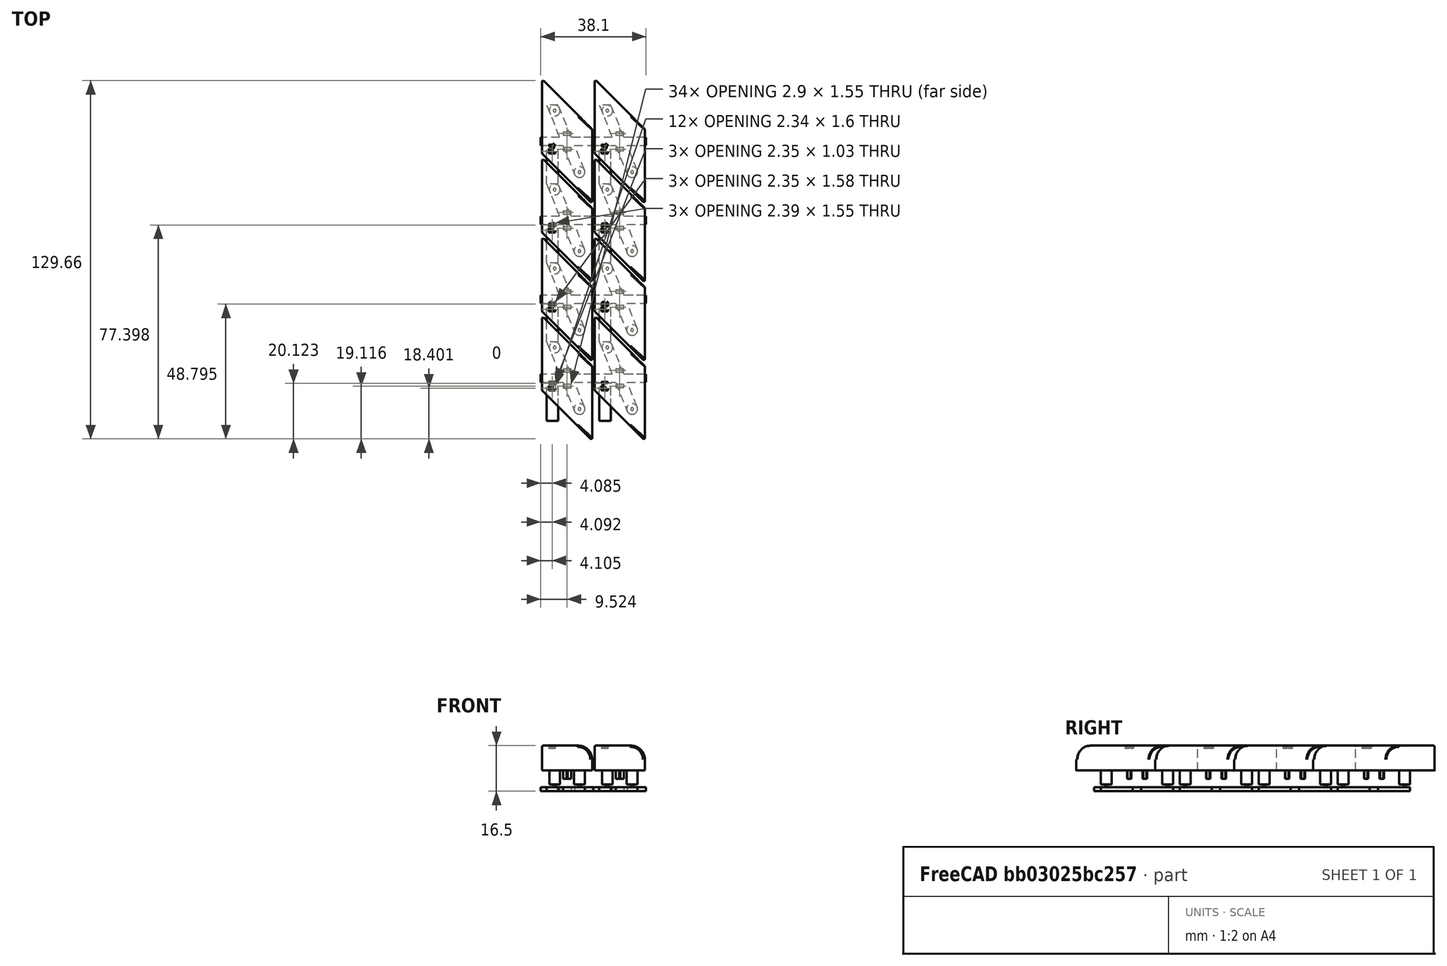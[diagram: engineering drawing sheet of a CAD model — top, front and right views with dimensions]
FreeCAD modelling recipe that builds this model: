
FCSTD DOCUMENT  (FreeCAD 0.21R33771 (Git))
Label: ConsoleXE-F1-4
License: All rights reserved
LicenseURL: http://en.wikipedia.org/wiki/All_rights_reserved
objects: Sketcher::SketchObject×6, PartDesign::Pad×5, Part::Extrusion×5, Part::FeaturePython×4, Part::Compound×4, Part::Part2DObjectPython×4, PartDesign::Body×2, PartDesign::Pocket×1, PartDesign::Line×1, PartDesign::Point×1, PartDesign::Fillet×1, PartDesign::FeatureBase×1, Part::Cut×1, Mesh::Feature×1
note: 43 computed .brp shape members not serialized (recipe doc carries the construction recipe); baked Part::Feature solids carry a one-line shape summary decoded from their .brp

FEATURE [Sketcher::SketchObject] Sketch  label="SideSketch"
  FullyConstrained = true
  MapMode = 5
  Placement = pos=(0,0,0) rot=(1,0,0;1.5708rad)
  Support = -> [XZ_Plane]
  expr: Constraints[10] = 26.4 * cos(45) - 0.5
  sketch-geometry (5):
    g0: LineSegment StartX=0 StartY=0 StartZ=0 EndX=0 EndY=9 EndZ=0
    g1: LineSegment StartX=0 StartY=9 StartZ=0 EndX=13.1676 EndY=9 EndZ=0
    g2: ArcOfCircle CenterX=13.1676 CenterY=4 CenterZ=0 NormalX=0 NormalY=0 NormalZ=1 AngleXU=0 Radius=5 StartAngle=0 EndAngle=1.5708
    g3: LineSegment StartX=18.1676 StartY=4 StartZ=0 EndX=18.1676 EndY=0 EndZ=0
    g4: LineSegment StartX=18.1676 StartY=0 StartZ=0 EndX=0 EndY=0 EndZ=0
  constraints (14):
    c: Coincident(g-1,g0)
    c: PointOnObject(g0,g-2)
    c: Coincident(g0,g1)
    c: Horizontal(g1)
    c: Tangent(g1,g2) = 1.5708
    c: Coincident(g2,g3)
    c: PointOnObject(g3,g-1)
    c: Vertical(g3)
    c: Coincident(g3,g4)
    c: Coincident(g4,g0)
    c: DistanceX(g4,g4) = 18.1676
    c: Horizontal(g2,g2)
    c: Radius(g2) = 5
    c: DistanceY(g0,g0) = 9
FEATURE [PartDesign::Pad] Pad  label="MainPad"
  Direction = (0,-1,-2e-16)
  Length = 45.0676
  Length2 = 10
  Placement = pos=(0,0,0) rot=(1,0,0;1.5708rad)
  Profile = -> Sketch
  ReferenceAxis = -> Sketch [N_Axis]
  Type = 0
  expr: Length = 26.4 mm * (1 + cos(45))
FEATURE [Sketcher::SketchObject] Sketch001  label="RemoveSidesSketch"
  ExternalGeometry = -> [Pad]
  FullyConstrained = true
  MapMode = 5
  Placement = pos=(0,0,0) rot=(1,0,0;3.14159rad)
  sketch-geometry (6):
    g0: LineSegment StartX=0 StartY=0 StartZ=0 EndX=18.1676 EndY=0 EndZ=0
    g1: LineSegment StartX=18.1676 StartY=0 StartZ=0 EndX=18.1676 EndY=18.1676 EndZ=0
    g2: LineSegment StartX=18.1676 StartY=18.1676 StartZ=0 EndX=0 EndY=0 EndZ=0
    g3: LineSegment StartX=18.1676 StartY=45.0676 StartZ=0 EndX=0 EndY=26.9 EndZ=0
    g4: LineSegment StartX=0 StartY=26.9 StartZ=0 EndX=0 EndY=45.0676 EndZ=0
    g5: LineSegment StartX=0 StartY=45.0676 StartZ=0 EndX=18.1676 EndY=45.0676 EndZ=0
  constraints (15):
    c: Coincident(g-1,g0)
    c: Coincident(g0,g1)
    c: Vertical(g1)
    c: Coincident(g1,g2)
    c: Coincident(g2,g0)
    c: Angle(g0,g2) = 0.785398
    c: Coincident(g3,g-3)
    c: PointOnObject(g3,g-2)
    c: Coincident(g3,g4)
    c: PointOnObject(g4,g-2)
    c: Coincident(g4,g5)
    c: Coincident(g5,g3)
    c: Horizontal(g5)
    c: Angle(g5,g3) = 0.785398
    c: Coincident(g0,g-4)
FEATURE [PartDesign::Pocket] Pocket  label="RemoveSidesPocket"
  BaseFeature = -> Pad
  Direction = (0,0,1)
  Length = 5
  Length2 = 5
  Placement = pos=(0,0,0) rot=(1,0,0;1.5708rad)
  Profile = -> Sketch001
  ReferenceAxis = -> Sketch001 [N_Axis]
  Type = 1
FEATURE [Sketcher::SketchObject] Sketch002  label="StabilizerPillarSketch"
  ExternalGeometry = -> [Pocket]
  FullyConstrained = true
  MapMode = 5
  Placement = pos=(0,0,0) rot=(1,0,0;3.14159rad)
  Support = -> [Pocket]
  sketch-geometry (4):
    g0: Circle CenterX=4.59721 CenterY=11.4041 CenterZ=0 NormalX=0 NormalY=0 NormalZ=1 AngleXU=0 Radius=1.95
    g1: Circle CenterX=13.5704 CenterY=33.6635 CenterZ=0 NormalX=0 NormalY=0 NormalZ=1 AngleXU=0 Radius=1.95
    g2: GeomPoint X=9.08381 Y=22.5338 Z=0
    g3: LineSegment StartX=0 StartY=0 StartZ=0 EndX=18.1676 EndY=45.0676 EndZ=0
  constraints (8):
    c: Symmetric(g0,g1,g2)
    c: Symmetric(g-3,g-1,g2)
    c: Coincident(g3,g-1)
    c: Coincident(g3,g-3)
    c: PointOnObject(g1,g3)
    c: Equal(g1,g0)
    c: Diameter(g1) = 3.9
    c: Distance(g0,g1) = 24
FEATURE [PartDesign::Pad] Pad001  label="StabilizerPillars"
  BaseFeature = -> Pocket
  Direction = (0,2e-16,-1)
  Length = 5
  Length2 = 10
  Placement = pos=(0,0,0) rot=(1,0,0;1.5708rad)
  Profile = -> Sketch002
  ReferenceAxis = -> Sketch002 [N_Axis]
  Type = 0
FEATURE [Sketcher::SketchObject] Sketch003  label="ChocV1Sketch"
  ExternalGeometry = -> [Pocket]
  FullyConstrained = true
  MapMode = 5
  Placement = pos=(0,0,0) rot=(1,0,0;3.14159rad)
  Support = -> [Pocket]
  sketch-geometry (26):
    g0: GeomPoint X=9.08381 Y=22.5338 Z=0
    g1: LineSegment StartX=10.5338 StartY=25.9588 StartZ=0 EndX=10.5338 EndY=24.8088 EndZ=0
    g2: LineSegment StartX=7.63381 StartY=24.8088 StartZ=0 EndX=7.63381 EndY=25.9588 EndZ=0
    g3: LineSegment StartX=10.5338 StartY=20.2588 StartZ=0 EndX=10.5338 EndY=19.1088 EndZ=0
    g4: LineSegment StartX=7.63381 StartY=19.1088 StartZ=0 EndX=7.63381 EndY=20.2588 EndZ=0
    g5: LineSegment StartX=7.63381 StartY=25.9588 StartZ=0 EndX=8.88381 EndY=25.9588 EndZ=0
    g6: LineSegment StartX=9.28381 StartY=25.9588 StartZ=0 EndX=10.5338 EndY=25.9588 EndZ=0
    g7: LineSegment StartX=8.88381 StartY=24.8088 StartZ=0 EndX=7.63381 EndY=24.8088 EndZ=0
    g8: LineSegment StartX=10.5338 StartY=24.8088 StartZ=0 EndX=9.28381 EndY=24.8088 EndZ=0
    g9: LineSegment StartX=7.63381 StartY=20.2588 StartZ=0 EndX=8.88381 EndY=20.2588 EndZ=0
    g10: LineSegment StartX=9.28381 StartY=20.2588 StartZ=0 EndX=10.5338 EndY=20.2588 EndZ=0
    g11: LineSegment StartX=8.88381 StartY=19.1088 StartZ=0 EndX=7.63381 EndY=19.1088 EndZ=0
    g12: LineSegment StartX=10.5338 StartY=19.1088 StartZ=0 EndX=9.28381 EndY=19.1088 EndZ=0
    g13: GeomPoint X=9.08381 Y=25.3838 Z=0
    g14: LineSegment StartX=8.88381 StartY=20.2588 StartZ=0 EndX=8.88381 EndY=20.4588 EndZ=0
    g15: LineSegment StartX=8.88381 StartY=20.4588 StartZ=0 EndX=9.28381 EndY=20.4588 EndZ=0
    g16: LineSegment StartX=9.28381 StartY=20.4588 StartZ=0 EndX=9.28381 EndY=20.2588 EndZ=0
    g17: LineSegment StartX=8.88381 StartY=19.1088 StartZ=0 EndX=8.88381 EndY=18.9088 EndZ=0
    g18: LineSegment StartX=8.88381 StartY=18.9088 StartZ=0 EndX=9.28381 EndY=18.9088 EndZ=0
    g19: LineSegment StartX=9.28381 StartY=18.9088 StartZ=0 EndX=9.28381 EndY=19.1088 EndZ=0
    g20: LineSegment StartX=8.88381 StartY=24.8088 StartZ=0 EndX=8.88381 EndY=24.6088 EndZ=0
    g21: LineSegment StartX=8.88381 StartY=24.6088 StartZ=0 EndX=9.28381 EndY=24.6088 EndZ=0
    g22: LineSegment StartX=9.28381 StartY=24.6088 StartZ=0 EndX=9.28381 EndY=24.8088 EndZ=0
    g23: LineSegment StartX=8.88381 StartY=25.9588 StartZ=0 EndX=8.88381 EndY=26.1588 EndZ=0
    g24: LineSegment StartX=8.88381 StartY=26.1588 StartZ=0 EndX=9.28381 EndY=26.1588 EndZ=0
    g25: LineSegment StartX=9.28381 StartY=26.1588 StartZ=0 EndX=9.28381 EndY=25.9588 EndZ=0
  constraints (72):
    c: Symmetric(g-3,g-1,g0)
    c: Coincident(g6,g1)
    c: Coincident(g1,g8)
    c: Coincident(g7,g2)
    c: Coincident(g2,g5)
    c: Vertical(g1)
    c: Vertical(g2)
    c: Coincident(g10,g3)
    c: Coincident(g3,g12)
    c: Coincident(g11,g4)
    c: Coincident(g4,g9)
    c: Vertical(g3)
    c: Vertical(g4)
    c: DistanceY(g1,g1) = 1.15
    c: Equal(g1,g3)
    c: DistanceX(g5,g6) = 2.9
    c: Vertical(g7,g9)
    c: Vertical(g1,g10)
    c: Symmetric(g7,g10,g0)
    c: DistanceY(g11,g7) = 5.7
    c: Horizontal(g5)
    c: Horizontal(g6)
    c: Horizontal(g7)
    c: Horizontal(g8)
    c: Horizontal(g9)
    c: Horizontal(g10)
    c: Horizontal(g11)
    c: Horizontal(g12)
    c: Vertical(g5,g7)
    c: Vertical(g5,g9)
    c: Vertical(g5,g11)
    c: DistanceX(g11,g12) = 0.4
    c: Symmetric(g5,g8,g13)
    c: Symmetric(g2,g1,g13)
    c: Coincident(g9,g14)
    c: Vertical(g14)
    c: Coincident(g14,g15)
    c: Horizontal(g15)
    c: Coincident(g15,g16)
    c: Coincident(g16,g10)
    c: Vertical(g16)
    c: Coincident(g11,g17)
    c: Vertical(g17)
    c: Coincident(g17,g18)
    c: Horizontal(g18)
    c: Coincident(g18,g19)
    c: Coincident(g19,g12)
    c: Vertical(g19)
    c: Coincident(g7,g20)
    c: Vertical(g20)
    c: Coincident(g20,g21)
    c: Horizontal(g21)
    c: Coincident(g21,g22)
    c: Coincident(g22,g8)
    c: Vertical(g22)
    c: Coincident(g5,g23)
    c: Vertical(g23)
    c: Coincident(g23,g24)
    c: Horizontal(g24)
    c: Coincident(g24,g25)
    c: Coincident(g25,g6)
    c: Vertical(g25)
    c: Vertical(g6,g8)
    c: Vertical(g15,g18)
    c: Vertical(g15,g21)
    c: Horizontal(g7,g8)
    c: Horizontal(g11,g12)
    c: Horizontal(g9,g10)
    c: DistanceY(g18,g12) = 0.2
    c: Equal(g19,g16)
    c: Equal(g19,g22)
    c: Equal(g22,g25)
FEATURE [PartDesign::Pad] Pad002  label="ChocV1Pad"
  BaseFeature = -> Pad001
  Direction = (0,2e-16,-1)
  Length = 3
  Length2 = 10
  Placement = pos=(0,0,0) rot=(1,0,0;1.5708rad)
  Profile = -> Sketch003
  ReferenceAxis = -> Sketch003 [N_Axis]
  Type = 0
FEATURE [Sketcher::SketchObject] Sketch004  label="SupportSketch"
  ExternalGeometry = -> [Pad002]
  FullyConstrained = true
  MapMode = 5
  Placement = pos=(0,0,-5) rot=(1,0,0;3.14159rad)
  Support = -> [Pad002]
  sketch-geometry (2):
    g0: Circle CenterX=13.5704 CenterY=33.6635 CenterZ=0 NormalX=0 NormalY=0 NormalZ=1 AngleXU=0 Radius=0.5
    g1: Circle CenterX=4.59721 CenterY=11.4041 CenterZ=0 NormalX=0 NormalY=0 NormalZ=1 AngleXU=0 Radius=0.5
  constraints (4):
    c: Coincident(g0,g-4)
    c: Coincident(g1,g-3)
    c: Equal(g0,g1)
    c: Diameter(g0) = 1
FEATURE [PartDesign::Pad] Pad003  label="SupportPad"
  BaseFeature = -> Pad002
  Direction = (0,2e-16,-1)
  Length = 1
  Length2 = 10
  Placement = pos=(0,0,0) rot=(1,0,0;1.5708rad)
  Profile = -> Sketch004
  ReferenceAxis = -> Sketch004 [N_Axis]
  Type = 0
FEATURE [Sketcher::SketchObject] Sketch005  label="PlatformSketch"
  ExternalGeometry = -> [Pad003]
  FullyConstrained = true
  MapMode = 5
  Placement = pos=(2.2e-15,8e-16,-6) rot=(1,0,0;3.14159rad)
  Support = -> [Pad003]
  expr: Constraints[31] = 19.05 * 1.5
  sketch-geometry (19):
    g0: GeomPoint X=9.08381 Y=22.5338 Z=0
    g1: LineSegment StartX=5.91361 StartY=9.4541 StartZ=0 EndX=1.70865 EndY=9.4541 EndZ=0
    g2: GeomPoint X=9.08381 Y=22.5338 Z=0
    g3: LineSegment StartX=18.6088 StartY=24.0338 StartZ=0 EndX=18.6088 EndY=21.0338 EndZ=0
    g4: LineSegment StartX=-0.44119 StartY=21.0338 StartZ=0 EndX=-0.44119 EndY=24.0338 EndZ=0
    g5: GeomPoint X=9.08381 Y=22.5338 Z=0
    g6: LineSegment StartX=15.379 StartY=32.9344 StartZ=0 EndX=11.791 EndY=24.0338 EndZ=0
    g7: LineSegment StartX=18.6088 StartY=21.0338 StartZ=0 EndX=10.5816 EndY=21.0338 EndZ=0
    g8: LineSegment StartX=6.37665 StartY=21.0338 StartZ=0 EndX=-0.44119 EndY=21.0338 EndZ=0
    g9: LineSegment StartX=11.791 StartY=24.0338 StartZ=0 EndX=18.6088 EndY=24.0338 EndZ=0
    g10: LineSegment StartX=10.5816 StartY=21.0338 StartZ=0 EndX=5.91361 EndY=9.4541 EndZ=0
    g11: LineSegment StartX=1.70865 StartY=9.4541 StartZ=0 EndX=6.37665 EndY=21.0338 EndZ=0
    g12: LineSegment StartX=1.70865 StartY=38.0291 StartZ=0 EndX=5.91361 EndY=38.0291 EndZ=0
    g13: LineSegment StartX=7.58601 StartY=24.0338 StartZ=0 EndX=11.7618 EndY=34.3926 EndZ=0
    g14: ArcOfCircle CenterX=13.5704 CenterY=33.6635 CenterZ=0 NormalX=0 NormalY=0 NormalZ=1 AngleXU=0 Radius=1.95 StartAngle=5.89999 EndAngle=9.04159
    g15: LineSegment StartX=-0.44119 StartY=24.0338 StartZ=0 EndX=1.70865 EndY=24.0338 EndZ=0
    g16: LineSegment StartX=5.91361 StartY=24.0338 StartZ=0 EndX=7.58601 EndY=24.0338 EndZ=0
    g17: LineSegment StartX=1.70865 StartY=38.0291 StartZ=0 EndX=1.70865 EndY=24.0338 EndZ=0
    g18: LineSegment StartX=5.91361 StartY=38.0291 StartZ=0 EndX=5.91361 EndY=24.0338 EndZ=0
  constraints (49):
    c: Symmetric(g-4,g-3,g0)
    c: Coincident(g10,g1)
    c: Coincident(g1,g11)
    c: Coincident(g2,g0)
    c: Coincident(g3,g7)
    c: Coincident(g8,g4)
    c: Coincident(g4,g15)
    c: Coincident(g9,g3)
    c: Vertical(g3)
    c: Vertical(g4)
    c: Symmetric(g8,g3,g5)
    c: Coincident(g5,g0)
    c: DistanceY(g3,g3) = 3
    c: DistanceX(g15,g9) = 19.05
    c: Tangent(g6,g-4)
    c: Horizontal(g7)
    c: Horizontal(g8)
    c: Horizontal(g9)
    c: Horizontal(g8,g7)
    c: Horizontal(g16,g6)
    c: Coincident(g6,g9)
    c: Coincident(g16,g13)
    c: Coincident(g8,g11)
    c: Coincident(g7,g10)
    c: Tangent(g10,g-4)
    c: Horizontal(g12,g12)
    c: Equal(g12,g1)
    c: Vertical(g12,g1)
    c: PointOnObject(g8,g13)
    c: PointOnObject(g7,g6)
    c: Parallel(g11,g10)
    c: DistanceY(g1,g12) = 28.575
    c: Tangent(g1,g-4)
    c: Horizontal(g1)
    c: Tangent(g13,g-3) = 1.5708
    c: Coincident(g14,g-3)
    c: Coincident(g14,g13)
    c: Horizontal(g15)
    c: Horizontal(g16)
    c: Coincident(g17,g12)
    c: Coincident(g17,g15)
    c: Vertical(g17)
    c: Coincident(g18,g12)
    c: Vertical(g18)
    c: Horizontal(g15,g16)
    c: Coincident(g18,g16)
    c: Tangent(g11,g-4)
    c: Coincident(g14,g6)
    c: Tangent(g6,g-3)
FEATURE [PartDesign::Pad] Pad004  label="Platform"
  BaseFeature = -> Pad003
  Direction = (4e-16,4e-16,-1)
  Length = 1.5
  Length2 = 10
  Placement = pos=(0,0,0) rot=(1,0,0;1.5708rad)
  Profile = -> Sketch005
  ReferenceAxis = -> Sketch005 [N_Axis]
  Type = 0
FEATURE [Part::FeaturePython] LinearArray  # WARN: FeaturePython — macro-defined, semantics opaque (R4)
  Alignment = 0
  CellStart = A1
  Count = 4
  Dir = (0,1,0)
  DirIsDriven = true
  DistributionLaw = 0
  DrivenProperty = 1
  EndInclusive = true
  ExposePlacement = false
  GeneratorMode = 1
  MarkerShape = 1
  MarkerSize = 0
  NumElements = 4
  OrientMode = 0
  Point = (0,0,0)
  PointIsDriven = true
  Reverse = false
  SpanEnd = 50
  SpanStart = 0
  Step = 28.575
  Type = lattice2LinearArray.LinearArray
  VSGVersion = 1
  Values = 0.0 | 28.575000000000003 | 57.150000000000006 | 85.72500000000001
  ValuesSource = 2
  isLattice = 1
  expr: Step = 19.05 * 1.5
FEATURE [PartDesign::Line] DatumLine  label="TextTopDatumLine"
  AttacherType = Attacher::AttachEngineLine
  AttachmentOffset = pos=(2.3,0,0) rot=(0,0,1;0rad)
  Length = 20
  MapMode = 29
  Placement = pos=(2.3,1.8e-15,9) rot=(1,0,0;1.5708rad)
  ResizeMode = 0
  Support = -> [Pocket]
FEATURE [PartDesign::Point] DatumPoint  label="TextTopLeftDatumPoint"
  AttacherType = Attacher::AttachEnginePoint
  AttachmentOffset = pos=(2.3,0,0) rot=(0,0,1;0rad)
  MapMode = 37
  Placement = pos=(2.3,-26.9,9) rot=(0,0,1;0rad)
  Support = -> [Pocket]
FEATURE [Part::FeaturePython] LinearArray001  label="RowsArray"  # WARN: FeaturePython — macro-defined, semantics opaque (R4)
  Alignment = 0
  CellStart = A1
  Count = 2
  Dir = (1,0,0)
  DirIsDriven = true
  DistributionLaw = 0
  DrivenProperty = 1
  EndInclusive = true
  ExposePlacement = false
  GeneratorMode = 1
  MarkerShape = 1
  MarkerSize = 0
  NumElements = 2
  OrientMode = 1
  Point = (0,0,0)
  PointIsDriven = true
  Reverse = false
  SpanEnd = 50
  SpanStart = 0
  Step = 19.05
  Type = lattice2LinearArray.LinearArray
  VSGVersion = 1
  Values = 0.0 | 19.05
  ValuesSource = 2
  isLattice = 1
FEATURE [PartDesign::Fillet] Fillet
  Base = -> Pad004 [Edge89,Edge96,Edge95,Edge93,Edge92]
  BaseFeature = -> Pad004
  Placement = pos=(0,0,0) rot=(1,0,0;1.5708rad)
  Radius = 0.4
  SupportTransform = false
  UseAllEdges = false
FEATURE [PartDesign::Body] Body  label="ConsoleKeyBody"
  Group = -> [Sketch,Pad,Sketch001,Pocket,Sketch002,Pad001,Sketch003,Pad002,Sketch004,Pad003,Sketch005,Pad004,DatumLine,DatumPoint,Fillet]
  Origin = -> Origin
  Tip = -> Fillet
FEATURE [Part::Compound] Compound  label="ConsoleKeyCompound"
  Links = -> [Body,Fillet]
FEATURE [Part::FeaturePython] Populate  label="MainConsoleKeyArray"  # WARN: FeaturePython — macro-defined, semantics opaque (R4)
  Copying = 0
  ExposePlacement = false
  MarkerShape = 1
  MarkerSize = 0
  NumElements = 0
  Object = -> Compound
  OutputCompounding = 1
  PlacementsTo = -> LinearArray
  Referencing = 0
  Type = lattice2PopulateCopies.LatticePopulateCopies
  isLattice = 0
FEATURE [Part::Compound] Compound004  label="KeyRowCompound"
  Links = -> [Populate]
FEATURE [PartDesign::FeatureBase] BaseFeature
  BaseFeature = -> Populate
FEATURE [Part::Part2DObjectPython] ShapeString  label="F1ShapeString"  # Draft 2D object (typed FeaturePython)
  FontFile = <path>
  MakeFace = true
  Placement = pos=(4.82046,-27.1386,9) rot=(0,0,1;1.5708rad)
  Size = 2.5
  String = F1
  Tracking = 0
FEATURE [Part::Extrusion] Extrude  label="F1Extrude"
  Base = -> ShapeString
  Dir = (0,0,1)
  DirMode = 2
  FaceMakerClass = Part::FaceMakerBullseye
  LengthFwd = 0.5
  LengthRev = 0
  Reversed = true
  Solid = false
  Symmetric = false
FEATURE [Part::Part2DObjectPython] ShapeString001  label="F2ShapeString"  # Draft 2D object (typed FeaturePython)
  FontFile = <path>
  MakeFace = true
  Placement = pos=(4.82046,1.435,9) rot=(0,0,1;1.5708rad)
  Size = 2.5
  String = F2
  Tracking = 0
  expr: .Placement.Base.y = -27.14 + 1.5 * 19.05
FEATURE [Part::Extrusion] Extrude001  label="F2Extrude"
  Base = -> ShapeString001
  Dir = (0,0,1)
  DirMode = 2
  FaceMakerClass = Part::FaceMakerBullseye
  LengthFwd = 0.5
  LengthRev = 0
  Reversed = true
  Solid = false
  Symmetric = false
FEATURE [Part::Part2DObjectPython] ShapeString002  label="F3ShapeString"  # Draft 2D object (typed FeaturePython)
  FontFile = <path>
  MakeFace = true
  Placement = pos=(4.82046,30.01,9) rot=(0,0,1;1.5708rad)
  Size = 2.5
  String = F3
  Tracking = 0
  expr: .Placement.Base.y = -27.14 + 3 * 19.05
FEATURE [Part::Extrusion] Extrude002  label="F3Extrude"
  Base = -> ShapeString002
  Dir = (0,0,1)
  DirMode = 2
  FaceMakerClass = Part::FaceMakerBullseye
  LengthFwd = 0.5
  LengthRev = 0
  Reversed = true
  Solid = false
  Symmetric = false
FEATURE [Part::Part2DObjectPython] ShapeString003  label="F4ShapeString"  # Draft 2D object (typed FeaturePython)
  FontFile = <path>
  MakeFace = true
  Placement = pos=(4.82046,58.585,9) rot=(0,0,1;1.5708rad)
  Size = 2.5
  String = F4
  Tracking = 0
  expr: .Placement.Base.y = -27.14 + 4.5 * 19.05
FEATURE [Part::Extrusion] Extrude003  label="F4Extrude"
  Base = -> ShapeString003
  Dir = (0,0,1)
  DirMode = 2
  FaceMakerClass = Part::FaceMakerBullseye
  LengthFwd = 0.5
  LengthRev = 0
  Reversed = true
  Solid = false
  Symmetric = false
FEATURE [Part::Compound] Compound001  label="MainLegendsCompound"
  Links = -> [Extrude,Extrude001,Extrude002,Extrude003]
FEATURE [Part::Compound] Compound003  label="ShapeStringCompound"
  Links = -> [ShapeString,ShapeString001,ShapeString002,ShapeString003]
FEATURE [Part::Extrusion] Extrude004  label="LegendExtrude"
  Base = -> Compound003
  Dir = (0,0,1)
  DirMode = 2
  FaceMakerClass = Part::FaceMakerBullseye
  LengthFwd = 1
  LengthRev = 0
  Reversed = true
  Solid = false
  Symmetric = false
FEATURE [Part::Cut] Cut  label="KeyRowWithCutLegends"
  Base = -> Compound004
  Tool = -> Extrude004
FEATURE [Part::FeaturePython] Populate001  label="Populate RowsArray with KeyRowWithCutLegends"  # WARN: FeaturePython — macro-defined, semantics opaque (R4)
  Copying = 0
  ExposePlacement = false
  MarkerShape = 1
  MarkerSize = 0
  NumElements = 0
  Object = -> Cut
  OutputCompounding = 1
  PlacementsTo = -> LinearArray001
  Referencing = 0
  Type = lattice2PopulateCopies.LatticePopulateCopies
  isLattice = 0
FEATURE [PartDesign::Body] Body001  label="MainConsoleSet"
  BaseFeature = -> Populate
  Group = -> [BaseFeature]
  Origin = -> Origin001
  Tip = -> BaseFeature
FEATURE [Mesh::Feature] F1_4_ConsoleKeySet_x2  label="F1-4-ConsoleKeySet-x2"
note: 4 file-system paths scrubbed to <path> (originals preserved in the JSON sidecar)
